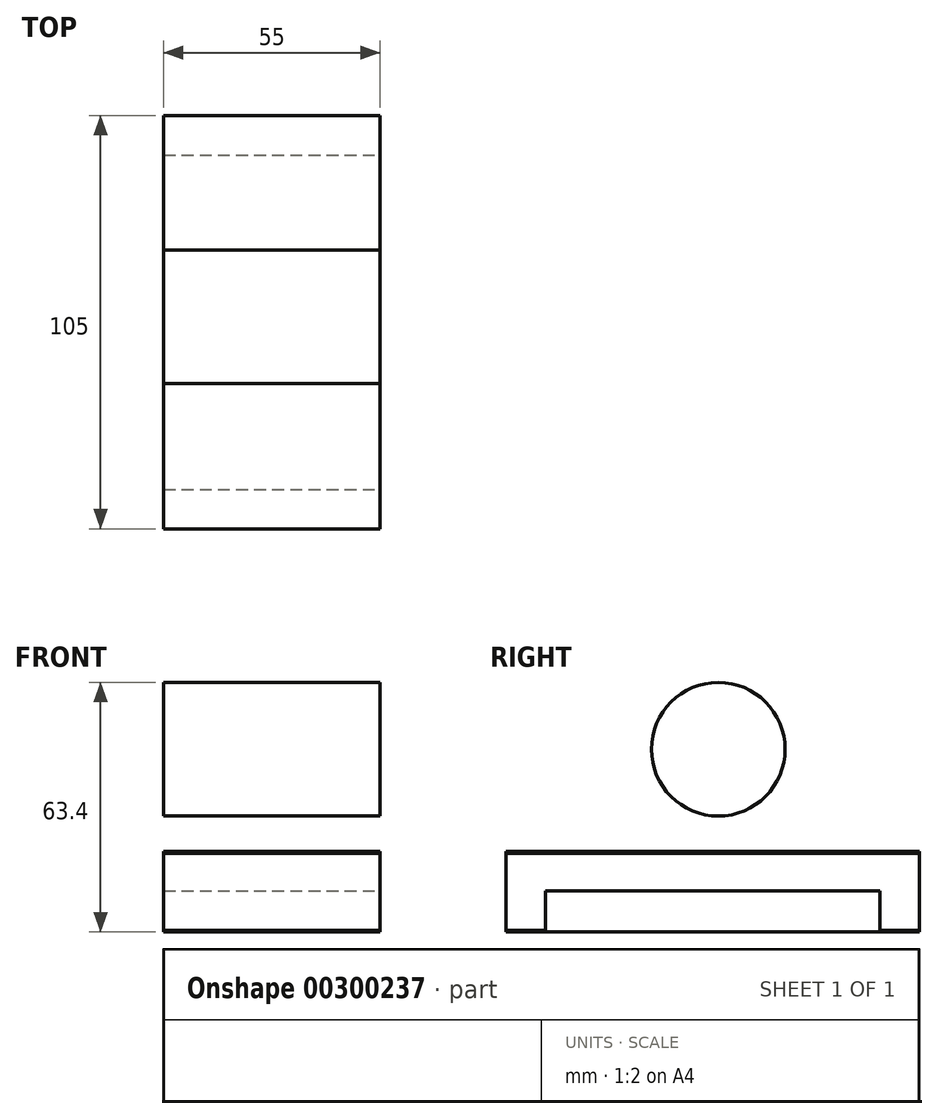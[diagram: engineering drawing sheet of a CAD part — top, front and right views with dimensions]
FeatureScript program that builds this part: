
annotation { "Feature Type Name" : "Feature", "Feature Type Description" : "" }
export const myFeature = defineFeature(function(context is Context, id is Id, definition is map)
    precondition{}
    {
        {
            var Q0;
            Q0=qCreatedBy(makeId("Front.planeOp"),FACE);
            var sketch = newSketch(context, id + "F0", { "sketchPlane" : qUnion([Q0])});
            skLineSegment(sketch, "E0.bottom", {"start": v(-55, -50) * mm, "end": v(0, -50) * mm});
            skLineSegment(sketch, "E0.top", {"start": v(-55, -30) * mm, "end": v(0, -30) * mm});
            skLineSegment(sketch, "E0.left", {"start": v(-55, -50) * mm, "end": v(-55, -30) * mm});
            skLineSegment(sketch, "E0.right", {"start": v(0, -50) * mm, "end": v(0, -30) * mm});
            skLineSegment(sketch, "E1.bottom", {"start": v(-50.05, -30) * mm, "end": v(-5.05, -30) * mm});
            skLineSegment(sketch, "E1.top", {"start": v(-50.05, 0) * mm, "end": v(-5.05, 0) * mm});
            skLineSegment(sketch, "E1.left", {"start": v(-50.05, -30) * mm, "end": v(-50.05, 0) * mm});
            skLineSegment(sketch, "E1.right", {"start": v(-5.05, -30) * mm, "end": v(-5.05, 0) * mm});
            skLineSegment(sketch, "E2", {"start": v(0, -50) * mm, "end": v(6.76, -42.63) * mm});
            skLineSegment(sketch, "E3", {"start": v(0, -30) * mm, "end": v(7.31, -23.18) * mm});
            skSolve(sketch);
        }
        {
            var Q0;
            Q0=makeQuery(id+"F0.imprint","IMPRINT",FACE,{"disambiguationData":[TD([[makeQuery(id+"F0.imprint","IMPRINT",EDGE,{"derivedFrom":sQuery(id+"F0.wireOp",EDGE,"E1.bottom")}),1.0]])]});
            var Q1;
            Q1=makeQuery(id+"F0.imprint","IMPRINT",FACE,{"disambiguationData":[TD([[makeQuery(id+"F0.imprint","IMPRINT",EDGE,{"derivedFrom":sQuery(id+"F0.wireOp",EDGE,"E0.bottom")}),1.0]])]});
            extrude(context, id + "F1", {"entities" : qUnion([Q0, Q1]), "oppositeDirection" : true, "depth" : 105 * mm});
        }
        {
            var Q0;
            Q0=qCreatedBy(makeId("Right.planeOp"),FACE);
            var sketch = newSketch(context, id + "F2", { "sketchPlane" : qUnion([Q0])});
            skLineSegment(sketch, "E4.bottom", {"start": v(0, -29.58) * mm, "end": v(10, -29.58) * mm});
            skLineSegment(sketch, "E4.top", {"start": v(0, -49.58) * mm, "end": v(10, -49.58) * mm});
            skLineSegment(sketch, "E4.left", {"start": v(0, -29.58) * mm, "end": v(0, -49.58) * mm});
            skLineSegment(sketch, "E4.right", {"start": v(10, -29.58) * mm, "end": v(10, -49.58) * mm});
            skPoint(sketch, "E5.oppositeSnap0", {"position": v(10, -39.58) * mm});
            skLineSegment(sketch, "E5.bottom", {"start": v(10, -29.58) * mm, "end": v(95, -29.58) * mm});
            skLineSegment(sketch, "E5.top", {"start": v(10, -39.58) * mm, "end": v(95, -39.58) * mm});
            skLineSegment(sketch, "E5.left", {"start": v(10, -29.58) * mm, "end": v(10, -39.58) * mm});
            skLineSegment(sketch, "E5.right", {"start": v(95, -29.58) * mm, "end": v(95, -39.58) * mm});
            skLineSegment(sketch, "E6.bottom", {"start": v(95, -29.58) * mm, "end": v(105, -29.58) * mm});
            skLineSegment(sketch, "E6.top", {"start": v(95, -49.58) * mm, "end": v(105, -49.58) * mm});
            skLineSegment(sketch, "E6.left", {"start": v(95, -29.58) * mm, "end": v(95, -49.58) * mm});
            skLineSegment(sketch, "E6.right", {"start": v(105, -29.58) * mm, "end": v(105, -49.58) * mm});
            skCircle(sketch, "E7", {"center": v(53.9, -3.58) * mm, "radius": 16.98 * mm});
            skSolve(sketch);
        }
        {
            var Q0;
            Q0 = qSketchRegion(id + "F2", true);
            extrude(context, id + "F3", {"entities" : qUnion([Q0]), "oppositeDirection" : true, "depth" : 55 * mm});
        }
    });
